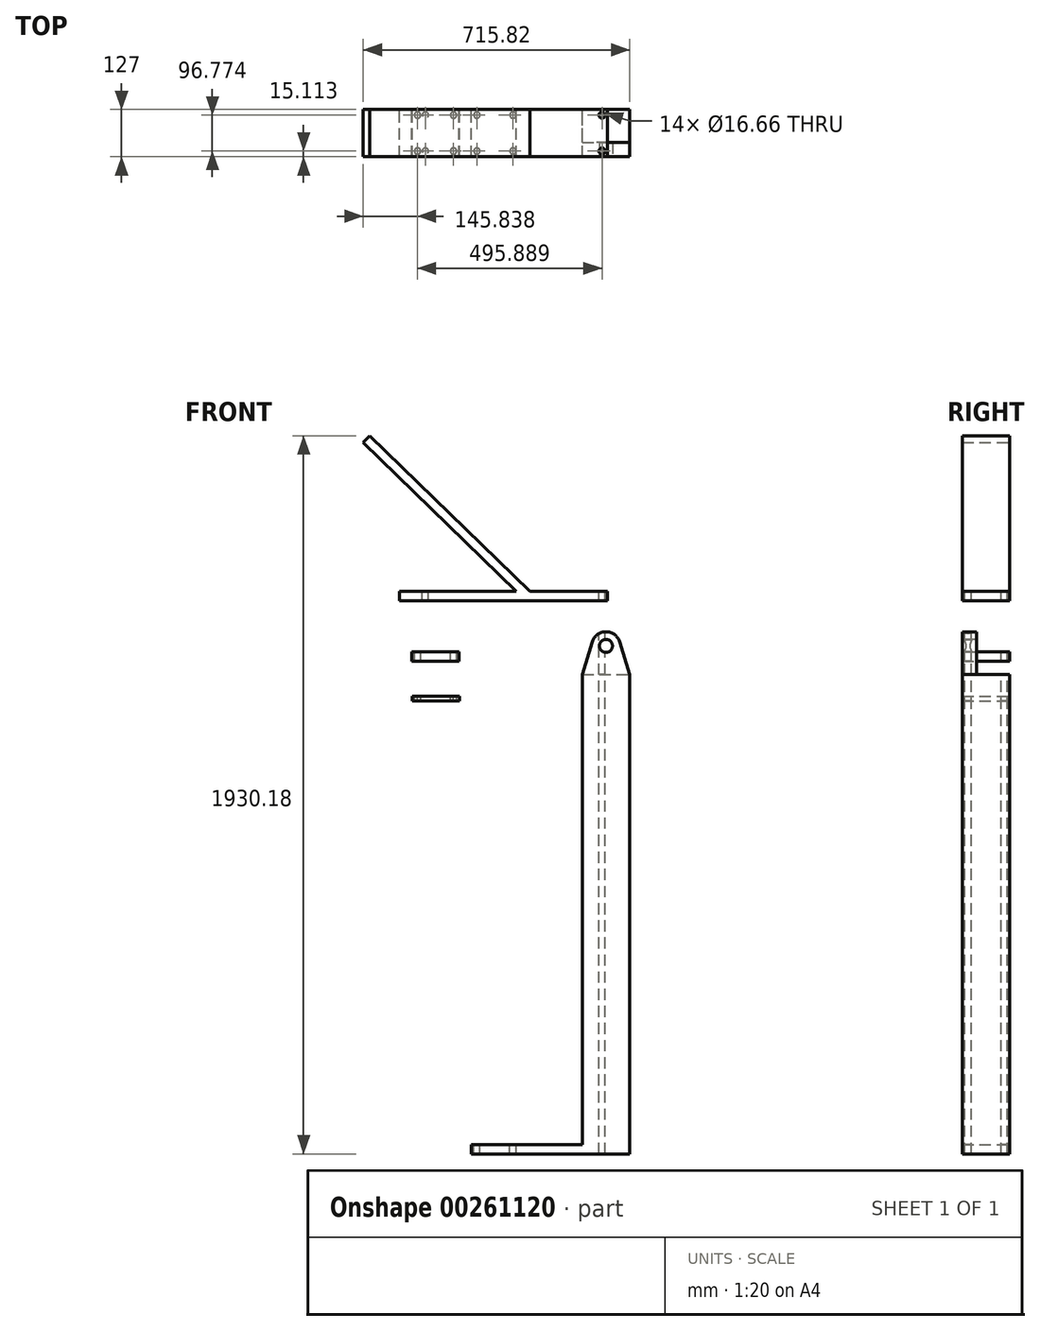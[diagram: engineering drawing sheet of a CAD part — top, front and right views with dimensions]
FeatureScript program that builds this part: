
annotation { "Feature Type Name" : "Feature", "Feature Type Description" : "" }
export const myFeature = defineFeature(function(context is Context, id is Id, definition is map)
    precondition{}
    {
        {
            var Q0;
            Q0=qCreatedBy(makeId("Front.planeOp"),FACE);
            var sketch = newSketch(context, id + "F0", { "sketchPlane" : qUnion([Q0])});
            skLineSegment(sketch, "E0", {"start": v(-298.45, 0) * mm, "end": v(0, 0) * mm});
            skLineSegment(sketch, "E1", {"start": v(0, 0) * mm, "end": v(0, 1263.65) * mm});
            skLineSegment(sketch, "E2", {"start": v(0, 1263.65) * mm, "end": v(127, 1263.65) * mm});
            skLineSegment(sketch, "E3", {"start": v(127, 1263.65) * mm, "end": v(127, -25.4) * mm});
            skLineSegment(sketch, "E4", {"start": v(127, -25.4) * mm, "end": v(-298.45, -25.4) * mm});
            skLineSegment(sketch, "E5", {"start": v(-298.45, -25.4) * mm, "end": v(-298.45, 0) * mm});
            skSolve(sketch);
        }
        {
            var Q0;
            Q0 = qSketchRegion(id + "F0", true);
            extrude(context, id + "F1", {"entities" : qUnion([Q0]), "endBound" : BoundingType.SYMMETRIC, "depth" : 127 * mm});
        }
        {
            var Q0;
            Q0=qCreatedBy(makeId("Right.planeOp"),FACE);
            cPlane(context, id + "F2", {"entities" : qUnion([Q0]), "cplaneType" : CPlaneType.OFFSET, "offset" : 234.95 * mm, "oppositeDirection" : true, "width" : 152.4 * mm, "height" : 152.4 * mm});
        }
        {
            var Q0;
            Q0=makeQuery(id+"F1.opExtrude","SWEPT_FACE",FACE,{"disambiguationData":[OSD([sQuery(id+"F0.wireOp",EDGE,"E0")])]});
            var sketch = newSketch(context, id + "F3", { "sketchPlane" : qUnion([Q0])});
            skCircle(sketch, "E6", {"center": v(-283.34, -48.39) * mm, "radius": 8.33 * mm});
            skCircle(sketch, "E7.MirrorC", {"center": v(-186.56, -48.39) * mm, "radius": 8.33 * mm});
            skCircle(sketch, "E8.MirrorC", {"center": v(-186.56, 48.39) * mm, "radius": 8.33 * mm});
            skCircle(sketch, "E9.MirrorC", {"center": v(-283.34, 48.39) * mm, "radius": 8.33 * mm});
            skSolve(sketch);
        }
        {
            var Q0;
            Q0 = qSketchRegion(id + "F3", true);
            extrude(context, id + "F4", {"entities" : qUnion([Q0]), "operationType" : NewBodyOperationType.REMOVE, "endBound" : BoundingType.THROUGH_ALL, "oppositeDirection" : true, "depth" : 25.4 * mm});
        }
        {
            var Q0;
            Q0=makeQuery(id+"F1.opExtrude","CAP_FACE",FACE,{"disambiguationData":[OSD([sQuery(id+"F0.wireOp",EDGE,"E0"),sQuery(id+"F0.wireOp",EDGE,"E1"),sQuery(id+"F0.wireOp",EDGE,"E2"),sQuery(id+"F0.wireOp",EDGE,"E3"),sQuery(id+"F0.wireOp",EDGE,"E4"),sQuery(id+"F0.wireOp",EDGE,"E5")])],"isStart":false});
            var sketch = newSketch(context, id + "F5", { "sketchPlane" : qUnion([Q0])});
            skCircle(sketch, "E10", {"center": v(63.5, 1339.85) * mm, "radius": 17.53 * mm});
            skArc(sketch, "E11", {"start": v(99.9, 1351.13) * mm, "mid": v(63.5, 1377.95) * mm, "end": v(27.1, 1351.13) * mm});
            skLineSegment(sketch, "E12", {"start": v(0, 1263.65) * mm, "end": v(27.1, 1351.13) * mm});
            skLineSegment(sketch, "E13", {"start": v(127, 1263.65) * mm, "end": v(99.9, 1351.13) * mm});
            skLineSegment(sketch, "E14", {"start": v(0, 1263.65) * mm, "end": v(127, 1263.65) * mm});
            skSolve(sketch);
        }
        {
            var Q0;
            Q0 = qSketchRegion(id + "F5", true);
            extrude(context, id + "F6", {"entities" : qUnion([Q0]), "operationType" : NewBodyOperationType.ADD, "oppositeDirection" : true, "depth" : 38.1 * mm});
        }
        {
            var Q0;
            Q0=qCreatedBy(makeId("Front.planeOp"),FACE);
            var sketch = newSketch(context, id + "F7", { "sketchPlane" : qUnion([Q0])});
            skLineSegment(sketch, "E15.bottom", {"start": v(-490.78, 1461.58) * mm, "end": v(68.02, 1461.58) * mm});
            skLineSegment(sketch, "E15.top", {"start": v(-490.78, 1486.98) * mm, "end": v(68.02, 1486.98) * mm});
            skLineSegment(sketch, "E15.left", {"start": v(-490.78, 1461.58) * mm, "end": v(-490.78, 1486.98) * mm});
            skLineSegment(sketch, "E15.right", {"start": v(68.02, 1461.58) * mm, "end": v(68.02, 1486.98) * mm});
            skSolve(sketch);
        }
        {
            var Q0;
            Q0 = qSketchRegion(id + "F7", true);
            extrude(context, id + "F8", {"entities" : qUnion([Q0]), "endBound" : BoundingType.SYMMETRIC, "depth" : 127 * mm});
        }
        {
            var Q0;
            Q0=makeQuery(id+"F8.opExtrude","SWEPT_FACE",FACE,{"disambiguationData":[OSD([sQuery(id+"F7.wireOp",EDGE,"E15.top")])]});
            var sketch = newSketch(context, id + "F9", { "sketchPlane" : qUnion([Q0])});
            skCircle(sketch, "E16", {"center": v(-421.7, -48.39) * mm, "radius": 8.33 * mm});
            skCircle(sketch, "E17", {"center": v(52.9, -48.39) * mm, "radius": 8.33 * mm});
            skCircle(sketch, "E18.MirrorC", {"center": v(52.9, 48.39) * mm, "radius": 8.33 * mm});
            skCircle(sketch, "E19.MirrorC", {"center": v(-421.7, 48.39) * mm, "radius": 8.33 * mm});
            skSolve(sketch);
        }
        {
            var Q0;
            Q0 = qSketchRegion(id + "F9", true);
            extrude(context, id + "F10", {"entities" : qUnion([Q0]), "operationType" : NewBodyOperationType.REMOVE, "endBound" : BoundingType.THROUGH_ALL, "oppositeDirection" : true, "depth" : 25.4 * mm});
        }
        {
            var Q0;
            Q0=qCreatedBy(makeId("Front.planeOp"),FACE);
            var sketch = newSketch(context, id + "F11", { "sketchPlane" : qUnion([Q0])});
            skLineSegment(sketch, "E20", {"start": v(-588.82, 1886.57) * mm, "end": v(-151.8, 1461.58) * mm});
            skLineSegment(sketch, "E21.0", {"start": v(-571.11, 1904.78) * mm, "end": v(-134.08, 1479.79) * mm});
            skLineSegment(sketch, "E22", {"start": v(-151.8, 1461.58) * mm, "end": v(-134.08, 1479.79) * mm});
            skLineSegment(sketch, "E23", {"start": v(-588.82, 1886.57) * mm, "end": v(-571.11, 1904.78) * mm});
            skSolve(sketch);
        }
        {
            var Q0;
            Q0 = qSketchRegion(id + "F11", true);
            extrude(context, id + "F12", {"entities" : qUnion([Q0]), "operationType" : NewBodyOperationType.ADD, "endBound" : BoundingType.SYMMETRIC, "depth" : 127 * mm});
        }
        {
            var Q0;
            Q0=qCreatedBy(makeId("Front.planeOp"),FACE);
            var sketch = newSketch(context, id + "F13", { "sketchPlane" : qUnion([Q0])});
            skLineSegment(sketch, "E24.bottom", {"start": v(-458.1, 1323.94) * mm, "end": v(-331.1, 1323.94) * mm});
            skLineSegment(sketch, "E24.top", {"start": v(-458.1, 1298.54) * mm, "end": v(-331.1, 1298.54) * mm});
            skLineSegment(sketch, "E24.left", {"start": v(-458.1, 1323.94) * mm, "end": v(-458.1, 1298.54) * mm});
            skLineSegment(sketch, "E24.right", {"start": v(-331.1, 1323.94) * mm, "end": v(-331.1, 1298.54) * mm});
            skLineSegment(sketch, "E25.bottom", {"start": v(-457.73, 1204.13) * mm, "end": v(-330.73, 1204.13) * mm});
            skLineSegment(sketch, "E25.top", {"start": v(-457.73, 1191.43) * mm, "end": v(-330.73, 1191.43) * mm});
            skLineSegment(sketch, "E25.left", {"start": v(-457.73, 1204.13) * mm, "end": v(-457.73, 1191.43) * mm});
            skLineSegment(sketch, "E25.right", {"start": v(-330.73, 1204.13) * mm, "end": v(-330.73, 1191.43) * mm});
            skSolve(sketch);
        }
        {
            var Q0;
            Q0 = qSketchRegion(id + "F13", true);
            extrude(context, id + "F14", {"entities" : qUnion([Q0]), "endBound" : BoundingType.SYMMETRIC, "depth" : 127 * mm});
        }
        {
            var Q0;
            Q0=makeQuery(id+"F14.opExtrude","SWEPT_FACE",FACE,{"disambiguationData":[OSD([sQuery(id+"F13.wireOp",EDGE,"E24.bottom")])]});
            var sketch = newSketch(context, id + "F15", { "sketchPlane" : qUnion([Q0])});
            skCircle(sketch, "E26", {"center": v(-442.98, -48.39) * mm, "radius": 8.33 * mm});
            skCircle(sketch, "E27.0.1.0", {"center": v(-442.98, 48.39) * mm, "radius": 8.33 * mm});
            skCircle(sketch, "E27.1.0.0", {"center": v(-346.2, -48.39) * mm, "radius": 8.33 * mm});
            skCircle(sketch, "E27.1.1.0", {"center": v(-346.2, 48.39) * mm, "radius": 8.33 * mm});
            skLineSegment(sketch, "E27.direction1", {"start": v(-442.98, -48.39) * mm, "end": v(-346.2, -48.39) * mm, "construction": true});
            skLineSegment(sketch, "E27.direction2", {"start": v(-442.98, -48.39) * mm, "end": v(-442.98, 48.39) * mm, "construction": true});
            skSolve(sketch);
        }
        {
            var Q0;
            Q0 = qSketchRegion(id + "F15", true);
            extrude(context, id + "F16", {"entities" : qUnion([Q0]), "operationType" : NewBodyOperationType.REMOVE, "oppositeDirection" : true, "depth" : 161.04 * mm});
        }
        {
            var Q0;
            Q0=makeQuery(id+"F14.opExtrude","SWEPT_FACE",FACE,{"disambiguationData":[OSD([sQuery(id+"F13.wireOp",EDGE,"E25.bottom")])]});
            var sketch = newSketch(context, id + "F17", { "sketchPlane" : qUnion([Q0])});
            skCircle(sketch, "E28", {"center": v(-442.62, -48.39) * mm, "radius": 8.33 * mm});
            skCircle(sketch, "E29.0.1.0", {"center": v(-442.62, 48.39) * mm, "radius": 8.33 * mm});
            skCircle(sketch, "E29.1.0.0", {"center": v(-345.84, -48.39) * mm, "radius": 8.33 * mm});
            skCircle(sketch, "E29.1.1.0", {"center": v(-345.84, 48.39) * mm, "radius": 8.33 * mm});
            skLineSegment(sketch, "E29.direction1", {"start": v(-442.62, -48.39) * mm, "end": v(-345.84, -48.39) * mm, "construction": true});
            skLineSegment(sketch, "E29.direction2", {"start": v(-442.62, -48.39) * mm, "end": v(-442.62, 48.39) * mm, "construction": true});
            skSolve(sketch);
        }
        {
            var Q0;
            Q0 = qSketchRegion(id + "F17", true);
            extrude(context, id + "F18", {"entities" : qUnion([Q0]), "operationType" : NewBodyOperationType.REMOVE, "oppositeDirection" : true, "depth" : 25.4 * mm});
        }
    });
